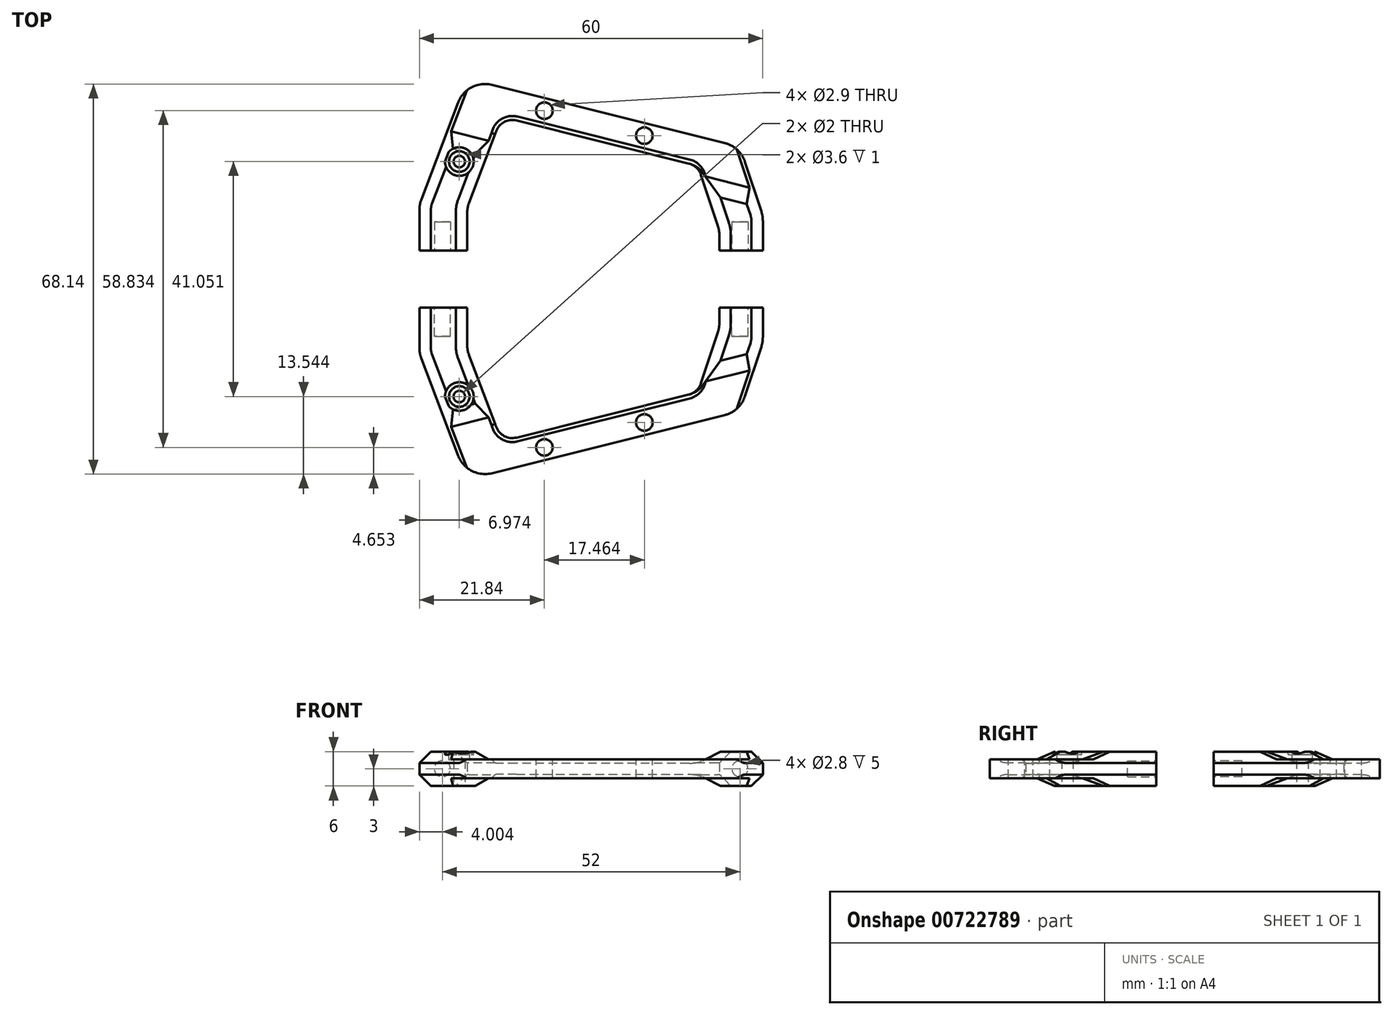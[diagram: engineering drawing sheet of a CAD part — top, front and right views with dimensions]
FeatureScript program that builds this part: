
annotation { "Feature Type Name" : "Feature", "Feature Type Description" : "" }
export const myFeature = defineFeature(function(context is Context, id is Id, definition is map)
    precondition{}
    {
        {
            var Q0;
            Q0=qCreatedBy(makeId("Top.planeOp"),FACE);
            var sketch = newSketch(context, id + "F0", { "sketchPlane" : qUnion([Q0])});
            skLineSegment(sketch, "E0", {"start": v(-36.57, -7.3) * mm, "end": v(-33.72, -7.3) * mm});
            skLineSegment(sketch, "E1", {"start": v(-38.07, -7.3) * mm, "end": v(-38.07, -2.3) * mm, "construction": true});
            skLineSegment(sketch, "E2", {"start": v(13.93, -7.3) * mm, "end": v(13.93, -2.3) * mm, "construction": true});
            skPoint(sketch, "E3", {"position": v(-12.07, -7.3) * mm});
            skLineSegment(sketch, "E4", {"start": v(-12.07, -7.3) * mm, "end": v(3.18, -7.3) * mm});
            skLineSegment(sketch, "E5", {"start": v(-12.07, -7.3) * mm, "end": v(-27.32, -7.3) * mm});
            skLineSegment(sketch, "E6", {"start": v(-42.07, -7.3) * mm, "end": v(-42.07, -0.22) * mm});
            skLineSegment(sketch, "E7", {"start": v(-41.74, 1.56) * mm, "end": v(-35.3, 18.55) * mm});
            skLineSegment(sketch, "E8", {"start": v(17.93, -7.3) * mm, "end": v(17.93, -2.1) * mm});
            skLineSegment(sketch, "E9", {"start": v(17.68, -0.54) * mm, "end": v(14.8, 8.2) * mm});
            skPoint(sketch, "E10", {"position": v(-27.32, -7.3) * mm});
            skPoint(sketch, "E11", {"position": v(3.18, -7.3) * mm});
            skLineSegment(sketch, "E12", {"start": v(-33.72, -7.3) * mm, "end": v(-33.72, -0.77) * mm});
            skLineSegment(sketch, "E13", {"start": v(-29.41, 21.62) * mm, "end": v(11.26, 11.47) * mm});
            skLineSegment(sketch, "E14.3", {"start": v(-25.1, 15.4) * mm, "end": v(5, 7.88) * mm});
            skLineSegment(sketch, "E15.0", {"start": v(-33.4, 1) * mm, "end": v(-28.64, 13.55) * mm});
            skLineSegment(sketch, "E16.0", {"start": v(10.09, -3.05) * mm, "end": v(7.13, 5.91) * mm});
            skPoint(sketch, "E17.visualSharp", {"position": v(-27.7, 16.04) * mm});
            skArc(sketch, "E17.filletArc", {"start": v(-25.1, 15.4) * mm, "mid": v(-27.22, 15.14) * mm, "end": v(-28.64, 13.55) * mm});
            skPoint(sketch, "E18.visualSharp", {"position": v(6.6, 7.48) * mm});
            skArc(sketch, "E18.filletArc", {"start": v(7.13, 5.91) * mm, "mid": v(6.32, 7.17) * mm, "end": v(5, 7.88) * mm});
            skPoint(sketch, "E19.visualSharp", {"position": v(13.93, 10.8) * mm});
            skArc(sketch, "E19.filletArc", {"start": v(14.8, 8.2) * mm, "mid": v(13.45, 10.29) * mm, "end": v(11.26, 11.47) * mm});
            skPoint(sketch, "E20.visualSharp", {"position": v(-33.72, 22.7) * mm});
            skArc(sketch, "E20.filletArc", {"start": v(-29.41, 21.62) * mm, "mid": v(-32.94, 21.2) * mm, "end": v(-35.3, 18.55) * mm});
            skPoint(sketch, "E21.visualSharp", {"position": v(-33.72, 0.14) * mm});
            skArc(sketch, "E21.filletArc", {"start": v(-33.4, 1) * mm, "mid": v(-33.64, 0.13) * mm, "end": v(-33.72, -0.77) * mm});
            skPoint(sketch, "E22.visualSharp", {"position": v(-42.07, 0.7) * mm});
            skArc(sketch, "E22.filletArc", {"start": v(-41.74, 1.56) * mm, "mid": v(-41.98, 0.68) * mm, "end": v(-42.07, -0.22) * mm});
            skPoint(sketch, "E23.visualSharp", {"position": v(17.93, -1.3) * mm});
            skArc(sketch, "E23.filletArc", {"start": v(17.93, -2.1) * mm, "mid": v(17.87, -1.31) * mm, "end": v(17.68, -0.54) * mm});
            skLineSegment(sketch, "E24", {"start": v(10.34, -4.61) * mm, "end": v(10.34, -7.3) * mm});
            skPoint(sketch, "E25.visualSharp", {"position": v(10.34, -3.81) * mm});
            skArc(sketch, "E25.filletArc", {"start": v(10.34, -4.61) * mm, "mid": v(10.27, -3.82) * mm, "end": v(10.09, -3.05) * mm});
            skLineSegment(sketch, "E26.trimOffspring", {"start": v(-33.72, -7.3) * mm, "end": v(-36.57, -7.3) * mm});
            skLineSegment(sketch, "E27.trimOffspring", {"start": v(10.34, -7.3) * mm, "end": v(12.43, -7.3) * mm});
            skLineSegment(sketch, "E28.trimOffspring", {"start": v(-27.32, -7.3) * mm, "end": v(3.18, -7.3) * mm});
            skPoint(sketch, "E29.middle", {"position": v(13.93, -7.3) * mm});
            skPoint(sketch, "E30.middle", {"position": v(-38.07, -7.3) * mm});
            skLineSegment(sketch, "E31.trimOffspring", {"start": v(15.43, -7.3) * mm, "end": v(17.93, -7.3) * mm});
            skLineSegment(sketch, "E32.trimOffspring", {"start": v(-39.57, -7.3) * mm, "end": v(-42.07, -7.3) * mm});
            skLineSegment(sketch, "E33", {"start": v(-39.57, -7.3) * mm, "end": v(-36.57, -7.3) * mm});
            skLineSegment(sketch, "E34", {"start": v(12.43, -7.3) * mm, "end": v(15.43, -7.3) * mm});
            skCircle(sketch, "E35", {"center": v(-35.1, 8.23) * mm, "radius": 1 * mm});
            skSolve(sketch);
        }
        {
            var Q0;
            Q0 = qSketchRegion(id + "F0", true);
            extrude(context, id + "F1", {"entities" : qUnion([Q0]), "depth" : 3.3 * mm, "offsetDistance" : 25 * mm});
        }
        {
            var Q0;
            Q0=makeQuery(id+"F1.opExtrude","CAP_FACE",FACE,{"disambiguationData":[OSD([sQuery(id+"F0.wireOp",EDGE,"E6"),sQuery(id+"F0.wireOp",EDGE,"E7"),sQuery(id+"F0.wireOp",EDGE,"E8"),sQuery(id+"F0.wireOp",EDGE,"E9"),sQuery(id+"F0.wireOp",EDGE,"E12"),sQuery(id+"F0.wireOp",EDGE,"E13"),sQuery(id+"F0.wireOp",EDGE,"m04gNwWP-YN1E-dRtR-cmD1-2egMuyUMC3tO"),sQuery(id+"F0.wireOp",EDGE,"E14.3"),sQuery(id+"F0.wireOp",EDGE,"E15.0"),sQuery(id+"F0.wireOp",EDGE,"E16.0"),sQuery(id+"F0.wireOp",EDGE,"E17.filletArc"),sQuery(id+"F0.wireOp",EDGE,"E18.filletArc"),sQuery(id+"F0.wireOp",EDGE,"E19.filletArc"),sQuery(id+"F0.wireOp",EDGE,"E20.filletArc"),sQuery(id+"F0.wireOp",EDGE,"E21.filletArc"),sQuery(id+"F0.wireOp",EDGE,"E22.filletArc"),sQuery(id+"F0.wireOp",EDGE,"E23.filletArc"),sQuery(id+"F0.wireOp",EDGE,"E24"),sQuery(id+"F0.wireOp",EDGE,"E25.filletArc"),sQuery(id+"F0.wireOp",EDGE,"E26.trimOffspring"),sQuery(id+"F0.wireOp",EDGE,"E27.trimOffspring"),sQuery(id+"F0.wireOp",EDGE,"E31.trimOffspring"),sQuery(id+"F0.wireOp",EDGE,"E32.trimOffspring"),sQuery(id+"F0.wireOp",EDGE,"E33"),sQuery(id+"F0.wireOp",EDGE,"E34")])],"isStart":false});
            cPlane(context, id + "F2", {"entities" : qUnion([Q0]), "cplaneType" : CPlaneType.OFFSET, "offset" : 1.65 * mm, "oppositeDirection" : true, "width" : 150 * mm, "height" : 150 * mm});
        }
        {
            var Q0;
            Q0=qCreatedBy(id+"F2.planeOp",FACE);
            var sketch = newSketch(context, id + "F3", { "sketchPlane" : qUnion([Q0])});
            skLineSegment(sketch, "E36.0", {"start": v(-41.74, 1.56) * mm, "end": v(-37.1, 13.77) * mm});
            skArc(sketch, "E36.1", {"start": v(-41.74, 1.56) * mm, "mid": v(-41.98, 0.68) * mm, "end": v(-42.07, -0.22) * mm});
            skLineSegment(sketch, "E36.2", {"start": v(-42.07, -7.3) * mm, "end": v(-42.07, -0.22) * mm});
            skLineSegment(sketch, "E36.3", {"start": v(-33.4, 1) * mm, "end": v(-29.3, 11.82) * mm});
            skArc(sketch, "E36.4", {"start": v(-33.4, 1) * mm, "mid": v(-33.64, 0.13) * mm, "end": v(-33.72, -0.77) * mm});
            skLineSegment(sketch, "E36.5", {"start": v(-33.72, -7.3) * mm, "end": v(-33.72, -0.77) * mm});
            skLineSegment(sketch, "E36.7", {"start": v(-33.72, -7.3) * mm, "end": v(-42.07, -7.3) * mm});
            skCircle(sketch, "E37.0", {"center": v(-35.1, 8.23) * mm, "radius": 1 * mm});
            skLineSegment(sketch, "E38.0", {"start": v(10.34, -4.61) * mm, "end": v(10.34, -7.3) * mm});
            skLineSegment(sketch, "E38.1", {"start": v(10.09, -3.05) * mm, "end": v(7.13, 5.91) * mm});
            skLineSegment(sketch, "E38.2", {"start": v(17.93, -7.3) * mm, "end": v(17.93, -2.1) * mm});
            skLineSegment(sketch, "E38.3", {"start": v(15.43, -7.3) * mm, "end": v(17.93, -7.3) * mm});
            skLineSegment(sketch, "E38.4", {"start": v(12.43, -7.3) * mm, "end": v(15.43, -7.3) * mm});
            skLineSegment(sketch, "E38.5", {"start": v(10.34, -7.3) * mm, "end": v(12.43, -7.3) * mm});
            skArc(sketch, "E38.6", {"start": v(10.34, -4.61) * mm, "mid": v(10.27, -3.82) * mm, "end": v(10.09, -3.05) * mm});
            skArc(sketch, "E38.7", {"start": v(17.93, -2.1) * mm, "mid": v(17.87, -1.31) * mm, "end": v(17.68, -0.54) * mm});
            skLineSegment(sketch, "E38.8", {"start": v(17.68, -0.54) * mm, "end": v(16.3, 3.62) * mm});
            skLineSegment(sketch, "E39.0", {"start": v(-25.1, 15.4) * mm, "end": v(5, 7.88) * mm});
            skLineSegment(sketch, "E40", {"start": v(-37.1, 13.77) * mm, "end": v(-29.3, 11.82) * mm});
            skLineSegment(sketch, "E41", {"start": v(7.13, 5.91) * mm, "end": v(16.3, 3.62) * mm});
            skPoint(sketch, "E42.orphan", {"position": v(14.8, 8.2) * mm});
            skSolve(sketch);
        }
        {
            var Q0;
            Q0 = qSketchRegion(id + "F3", true);
            extrude(context, id + "F4", {"entities" : qUnion([Q0]), "operationType" : NewBodyOperationType.ADD, "endBound" : BoundingType.SYMMETRIC, "depth" : 6 * mm, "offsetDistance" : 25 * mm});
        }
        {
            var Q0;
            Q0=makeQuery(id+"F1.opExtrude","SWEPT_FACE",FACE,{"disambiguationData":[OSD([sQuery(id+"F0.wireOp",EDGE,"E26.trimOffspring"),sQuery(id+"F0.wireOp",EDGE,"E32.trimOffspring"),sQuery(id+"F0.wireOp",EDGE,"E33")])]});
            var sketch = newSketch(context, id + "F5", { "sketchPlane" : qUnion([Q0])});
            skPoint(sketch, "E43.0", {"position": v(-38.07, 0) * mm});
            skCircle(sketch, "E44", {"center": v(-38.07, 1.65) * mm, "radius": 1.4 * mm});
            skPoint(sketch, "E45.0", {"position": v(-42.07, 1.65) * mm});
            skLineSegment(sketch, "E46", {"start": v(-38.07, 0) * mm, "end": v(-38.07, 4.65) * mm, "construction": true});
            skLineSegment(sketch, "E47", {"start": v(-42.07, 1.65) * mm, "end": v(-33.72, 1.65) * mm, "construction": true});
            skSolve(sketch);
        }
        {
            var Q0;
            {var subQ0=sQuery(id+"F5.wireOp",EDGE,"E44");var subQ1=sQuery(id+"F0.wireOp",EDGE,"E33");var subQ2=sQuery(id+"F0.wireOp",EDGE,"E32.trimOffspring");var subQ3=sQuery(id+"F0.wireOp",EDGE,"E26.trimOffspring");var subQ4=makeQuery(id+"F1.opExtrude","CAP_EDGE",EDGE,{"disambiguationData":[OSD([subQ3,subQ2,subQ1])],"isStart":false});var subQ5=makeQuery(id+"F5.imprint","INTERSECT",VERTEX,{"disambiguationData":[OD(0.0)],"derivedFrom":[subQ4,subQ0]});Q0=makeQuery(id+"F5.imprint","IMPRINT",FACE,{"disambiguationData":[TD([[makeQuery(id+"F5.imprint","IMPRINT",EDGE,{"disambiguationData":[TD([[subQ5,-1.0]])],"derivedFrom":subQ0}),1.0]])]});}
            extrude(context, id + "F6", {"entities" : qUnion([Q0]), "operationType" : NewBodyOperationType.REMOVE, "oppositeDirection" : true, "depth" : 5 * mm, "offsetDistance" : 25 * mm});
        }
        {
            var Q0;
            Q0=makeQuery(id+"F1.opExtrude","SWEPT_FACE",FACE,{"disambiguationData":[OSD([sQuery(id+"F0.wireOp",EDGE,"E27.trimOffspring"),sQuery(id+"F0.wireOp",EDGE,"E31.trimOffspring"),sQuery(id+"F0.wireOp",EDGE,"E34")])]});
            var sketch = newSketch(context, id + "F7", { "sketchPlane" : qUnion([Q0])});
            skPoint(sketch, "E48.0", {"position": v(13.93, 0) * mm});
            skLineSegment(sketch, "E49", {"start": v(13.93, 0) * mm, "end": v(13.93, 3.3) * mm, "construction": true});
            skCircle(sketch, "E50", {"center": v(13.93, 1.65) * mm, "radius": 1.4 * mm});
            skLineSegment(sketch, "E51", {"start": v(10.34, 1.65) * mm, "end": v(17.93, 1.65) * mm, "construction": true});
            skSolve(sketch);
        }
        {
            var Q0;
            Q0 = qSketchRegion(id + "F7", true);
            extrude(context, id + "F8", {"entities" : qUnion([Q0]), "operationType" : NewBodyOperationType.REMOVE, "oppositeDirection" : true, "depth" : 5 * mm, "offsetDistance" : 25 * mm});
        }
        {
            var Q0;
            Q0=makeQuery(id+"F4.opExtrude","CAP_EDGE",EDGE,{"disambiguationData":[OSD([sQuery(id+"F3.wireOp",EDGE,"E36.0")])],"isStart":true});
            var Q1;
            Q1=makeQuery(id+"F4.opExtrude","CAP_EDGE",EDGE,{"disambiguationData":[OSD([sQuery(id+"F3.wireOp",EDGE,"E36.0")])],"isStart":false});
            var Q2;
            Q2=makeQuery(id+"F4.opExtrude","CAP_EDGE",EDGE,{"disambiguationData":[OSD([sQuery(id+"F3.wireOp",EDGE,"E36.2")])],"isStart":false});
            var Q3;
            Q3=makeQuery(id+"F4.opExtrude","CAP_EDGE",EDGE,{"disambiguationData":[OSD([sQuery(id+"F3.wireOp",EDGE,"E36.2")])],"isStart":true});
            var Q4;
            Q4=makeQuery(id+"F4.opExtrude","CAP_EDGE",EDGE,{"disambiguationData":[OSD([sQuery(id+"F3.wireOp",EDGE,"E36.1")])],"isStart":true});
            var Q5;
            Q5=makeQuery(id+"F4.opExtrude","CAP_EDGE",EDGE,{"disambiguationData":[OSD([sQuery(id+"F3.wireOp",EDGE,"E36.1")])],"isStart":false});
            var Q6;
            Q6=makeQuery(id+"F4.opExtrude","CAP_EDGE",EDGE,{"disambiguationData":[OSD([sQuery(id+"F3.wireOp",EDGE,"E36.5")])],"isStart":true});
            var Q7;
            Q7=makeQuery(id+"F4.opExtrude","CAP_EDGE",EDGE,{"disambiguationData":[OSD([sQuery(id+"F3.wireOp",EDGE,"E36.4")])],"isStart":true});
            var Q8;
            Q8=makeQuery(id+"F4.opExtrude","CAP_EDGE",EDGE,{"disambiguationData":[OSD([sQuery(id+"F3.wireOp",EDGE,"E36.3")])],"isStart":true});
            var Q9;
            Q9=makeQuery(id+"F4.opExtrude","CAP_EDGE",EDGE,{"disambiguationData":[OSD([sQuery(id+"F3.wireOp",EDGE,"E36.5")])],"isStart":false});
            var Q10;
            Q10=makeQuery(id+"F4.opExtrude","CAP_EDGE",EDGE,{"disambiguationData":[OSD([sQuery(id+"F3.wireOp",EDGE,"E36.4")])],"isStart":false});
            var Q11;
            Q11=makeQuery(id+"F4.opExtrude","CAP_EDGE",EDGE,{"disambiguationData":[OSD([sQuery(id+"F3.wireOp",EDGE,"E36.3")])],"isStart":false});
            var Q12;
            Q12=makeQuery(id+"F4.opExtrude","CAP_EDGE",EDGE,{"disambiguationData":[OSD([sQuery(id+"F3.wireOp",EDGE,"E38.0")])],"isStart":true});
            var Q13;
            Q13=makeQuery(id+"F4.opExtrude","CAP_EDGE",EDGE,{"disambiguationData":[OSD([sQuery(id+"F3.wireOp",EDGE,"E38.2")])],"isStart":true});
            var Q14;
            Q14=makeQuery(id+"F4.opExtrude","CAP_EDGE",EDGE,{"disambiguationData":[OSD([sQuery(id+"F3.wireOp",EDGE,"E38.2")])],"isStart":false});
            var Q15;
            Q15=makeQuery(id+"F4.opExtrude","CAP_EDGE",EDGE,{"disambiguationData":[OSD([sQuery(id+"F3.wireOp",EDGE,"E38.0")])],"isStart":false});
            chamfer(context, id + "F9", {"entities" : qUnion([Q0, Q1, Q2, Q3, Q4, Q5, Q6, Q7, Q8, Q9, Q10, Q11, Q12, Q13, Q14, Q15]), "width" : 2 * mm, "tangentPropagation" : true});
        }
        {
            var Q0;
            Q0=makeQuery(id+"F4.opExtrude","CAP_EDGE",EDGE,{"disambiguationData":[OSD([sQuery(id+"F3.wireOp",EDGE,"E41")])],"isStart":true});
            var Q1;
            Q1=makeQuery(id+"F4.opExtrude","CAP_EDGE",EDGE,{"disambiguationData":[OSD([sQuery(id+"F3.wireOp",EDGE,"E40")])],"isStart":true});
            chamfer(context, id + "F10", {"entities" : qUnion([Q0, Q1]), "chamferType" : ChamferType.TWO_OFFSETS, "width1" : 3 * mm, "oppositeDirection" : false, "width2" : 1.4 * mm, "tangentPropagation" : true});
        }
        {
            var Q0;
            Q0=makeQuery(id+"F4.opExtrude","CAP_EDGE",EDGE,{"disambiguationData":[OSD([sQuery(id+"F3.wireOp",EDGE,"E40")])],"isStart":false});
            var Q1;
            Q1=makeQuery(id+"F4.opExtrude","CAP_EDGE",EDGE,{"disambiguationData":[OSD([sQuery(id+"F3.wireOp",EDGE,"E41")])],"isStart":false});
            chamfer(context, id + "F11", {"entities" : qUnion([Q0, Q1]), "chamferType" : ChamferType.TWO_OFFSETS, "width1" : 1.4 * mm, "oppositeDirection" : false, "width2" : 3 * mm, "tangentPropagation" : true});
        }
        {
            var Q0;
            Q0=makeQuery(id+"F1.opExtrude","CAP_EDGE",EDGE,{"disambiguationData":[OSD([sQuery(id+"F0.wireOp",EDGE,"E14.3")])],"isStart":false});
            var Q1;
            Q1=makeQuery(id+"F1.opExtrude","CAP_EDGE",EDGE,{"disambiguationData":[OSD([sQuery(id+"F0.wireOp",EDGE,"E14.3")])],"isStart":true});
            chamfer(context, id + "F12", {"entities" : qUnion([Q0, Q1]), "width" : .7 * mm, "tangentPropagation" : true});
        }
        {
            var Q0;
            Q0=makeQuery(id+"F4.opExtrude","CAP_FACE",FACE,{"disambiguationData":[OSD([sQuery(id+"F3.wireOp",EDGE,"E36.0"),sQuery(id+"F3.wireOp",EDGE,"E36.1"),sQuery(id+"F3.wireOp",EDGE,"E36.2"),sQuery(id+"F3.wireOp",EDGE,"E36.3"),sQuery(id+"F3.wireOp",EDGE,"E36.4"),sQuery(id+"F3.wireOp",EDGE,"E36.5"),sQuery(id+"F3.wireOp",EDGE,"E36.7"),sQuery(id+"F3.wireOp",EDGE,"E37.0"),sQuery(id+"F3.wireOp",EDGE,"E40")])],"isStart":false});
            var sketch = newSketch(context, id + "F13", { "sketchPlane" : qUnion([Q0])});
            skCircle(sketch, "E52", {"center": v(-35.1, 8.23) * mm, "radius": 2.5 * mm});
            skCircle(sketch, "E53", {"center": v(-35.1, 8.23) * mm, "radius": 1.8 * mm});
            skSolve(sketch);
        }
        {
            var Q0;
            Q0=makeQuery(id+"F1.opExtrude","CAP_FACE",FACE,{"disambiguationData":[OSD([sQuery(id+"F0.wireOp",EDGE,"E6"),sQuery(id+"F0.wireOp",EDGE,"E7"),sQuery(id+"F0.wireOp",EDGE,"E8"),sQuery(id+"F0.wireOp",EDGE,"E9"),sQuery(id+"F0.wireOp",EDGE,"E12"),sQuery(id+"F0.wireOp",EDGE,"E13"),sQuery(id+"F0.wireOp",EDGE,"E14.3"),sQuery(id+"F0.wireOp",EDGE,"E15.0"),sQuery(id+"F0.wireOp",EDGE,"E16.0"),sQuery(id+"F0.wireOp",EDGE,"E17.filletArc"),sQuery(id+"F0.wireOp",EDGE,"E18.filletArc"),sQuery(id+"F0.wireOp",EDGE,"E19.filletArc"),sQuery(id+"F0.wireOp",EDGE,"E20.filletArc"),sQuery(id+"F0.wireOp",EDGE,"E21.filletArc"),sQuery(id+"F0.wireOp",EDGE,"E22.filletArc"),sQuery(id+"F0.wireOp",EDGE,"E23.filletArc"),sQuery(id+"F0.wireOp",EDGE,"E24"),sQuery(id+"F0.wireOp",EDGE,"E25.filletArc"),sQuery(id+"F0.wireOp",EDGE,"E26.trimOffspring"),sQuery(id+"F0.wireOp",EDGE,"E27.trimOffspring"),sQuery(id+"F0.wireOp",EDGE,"E31.trimOffspring"),sQuery(id+"F0.wireOp",EDGE,"E32.trimOffspring"),sQuery(id+"F0.wireOp",EDGE,"E33"),sQuery(id+"F0.wireOp",EDGE,"E34"),sQuery(id+"F0.wireOp",EDGE,"E35")])],"isStart":false});
            var sketch = newSketch(context, id + "F14", { "sketchPlane" : qUnion([Q0])});
            skLineSegment(sketch, "E54", {"start": v(-20.23, 17.12) * mm, "end": v(-2.77, 12.76) * mm});
            skCircle(sketch, "E55", {"center": v(-20.23, 17.12) * mm, "radius": 1.45 * mm});
            skCircle(sketch, "E56", {"center": v(-2.77, 12.76) * mm, "radius": 1.45 * mm});
            skLineSegment(sketch, "E57", {"start": v(-15.94, 18.26) * mm, "end": v(-16.99, 14.1) * mm});
            skPoint(sketch, "E58", {"position": v(-16.46, 16.18) * mm});
            skLineSegment(sketch, "E59", {"start": v(-29.41, 21.62) * mm, "end": v(-30.5, 17.24) * mm});
            skSolve(sketch);
        }
        {
            var Q0;
            Q0=makeQuery(id+"F14.imprint","IMPRINT",FACE,{"disambiguationData":[TD([[makeQuery(id+"F14.imprint","IMPRINT",EDGE,{"derivedFrom":sQuery(id+"F14.wireOp",EDGE,"E55")}),1.0]])]});
            var Q1;
            Q1=makeQuery(id+"F14.imprint","IMPRINT",FACE,{"disambiguationData":[TD([[makeQuery(id+"F14.imprint","IMPRINT",EDGE,{"derivedFrom":sQuery(id+"F14.wireOp",EDGE,"E56")}),1.0]])]});
            extrude(context, id + "F15", {"entities" : qUnion([Q0, Q1]), "operationType" : NewBodyOperationType.REMOVE, "oppositeDirection" : true, "depth" : 25 * mm, "offsetDistance" : 25 * mm});
        }
        {
            var Q0;
            Q0=makeQuery(id+"F13.imprint","IMPRINT",FACE,{"disambiguationData":[TD([[makeQuery(id+"F13.imprint","IMPRINT",EDGE,{"derivedFrom":sQuery(id+"F13.wireOp",EDGE,"E53")}),-1.0]])]});
            var Q1;
            {var subQ0=sQuery(id+"F13.wireOp",EDGE,"E52");var subQ1=sQuery(id+"F3.wireOp",EDGE,"E36.0");var subQ2=makeQuery(id+"F9.opChamfer","BLEND_EDGE",EDGE,{"blendedFrom":[makeQuery(id+"F4.opExtrude","CAP_EDGE",EDGE,{"disambiguationData":[OSD([subQ1])],"isStart":false}),makeQuery(id+"F4.opExtrude","CAP_FACE",FACE,{"disambiguationData":[OSD([subQ1,sQuery(id+"F3.wireOp",EDGE,"E36.1"),sQuery(id+"F3.wireOp",EDGE,"E36.2"),sQuery(id+"F3.wireOp",EDGE,"E36.3"),sQuery(id+"F3.wireOp",EDGE,"E36.4"),sQuery(id+"F3.wireOp",EDGE,"E36.5"),sQuery(id+"F3.wireOp",EDGE,"E36.7"),sQuery(id+"F3.wireOp",EDGE,"E37.0"),sQuery(id+"F3.wireOp",EDGE,"E40")])],"isStart":false})],"blendedInto":[makeQuery(id+"F4.opExtrude","CAP_FACE",FACE,{"disambiguationData":[OSD([subQ1,sQuery(id+"F3.wireOp",EDGE,"E36.1"),sQuery(id+"F3.wireOp",EDGE,"E36.2"),sQuery(id+"F3.wireOp",EDGE,"E36.3"),sQuery(id+"F3.wireOp",EDGE,"E36.4"),sQuery(id+"F3.wireOp",EDGE,"E36.5"),sQuery(id+"F3.wireOp",EDGE,"E36.7"),sQuery(id+"F3.wireOp",EDGE,"E37.0"),sQuery(id+"F3.wireOp",EDGE,"E40")])],"isStart":false})]});var subQ3=makeQuery(id+"F13.imprint","INTERSECT",VERTEX,{"disambiguationData":[OD(0.0)],"derivedFrom":[subQ2,subQ0]});Q1=makeQuery(id+"F13.imprint","IMPRINT",FACE,{"disambiguationData":[TD([[makeQuery(id+"F13.imprint","IMPRINT",EDGE,{"disambiguationData":[TD([[subQ3,-1.0]])],"derivedFrom":subQ0}),1.0]])]});}
            var Q2;
            {var subQ0=sQuery(id+"F13.wireOp",EDGE,"E52");var subQ1=sQuery(id+"F3.wireOp",EDGE,"E40");var subQ2=makeQuery(id+"F11.opChamfer","BLEND_EDGE",EDGE,{"blendedFrom":[makeQuery(id+"F4.opExtrude","CAP_EDGE",EDGE,{"disambiguationData":[OSD([subQ1])],"isStart":false}),makeQuery(id+"F4.opExtrude","CAP_FACE",FACE,{"disambiguationData":[OSD([sQuery(id+"F3.wireOp",EDGE,"E36.0"),sQuery(id+"F3.wireOp",EDGE,"E36.1"),sQuery(id+"F3.wireOp",EDGE,"E36.2"),sQuery(id+"F3.wireOp",EDGE,"E36.3"),sQuery(id+"F3.wireOp",EDGE,"E36.4"),sQuery(id+"F3.wireOp",EDGE,"E36.5"),sQuery(id+"F3.wireOp",EDGE,"E36.7"),sQuery(id+"F3.wireOp",EDGE,"E37.0"),subQ1])],"isStart":false})],"blendedInto":[makeQuery(id+"F4.opExtrude","CAP_FACE",FACE,{"disambiguationData":[OSD([sQuery(id+"F3.wireOp",EDGE,"E36.0"),sQuery(id+"F3.wireOp",EDGE,"E36.1"),sQuery(id+"F3.wireOp",EDGE,"E36.2"),sQuery(id+"F3.wireOp",EDGE,"E36.3"),sQuery(id+"F3.wireOp",EDGE,"E36.4"),sQuery(id+"F3.wireOp",EDGE,"E36.5"),sQuery(id+"F3.wireOp",EDGE,"E36.7"),sQuery(id+"F3.wireOp",EDGE,"E37.0"),subQ1])],"isStart":false})]});var subQ3=makeQuery(id+"F13.imprint","INTERSECT",VERTEX,{"disambiguationData":[OD(0.0)],"derivedFrom":[subQ2,subQ0]});Q2=makeQuery(id+"F13.imprint","IMPRINT",FACE,{"disambiguationData":[TD([[makeQuery(id+"F13.imprint","IMPRINT",EDGE,{"disambiguationData":[TD([[subQ3,-1.0]])],"derivedFrom":subQ0}),1.0]])]});}
            var Q3;
            {var subQ0=sQuery(id+"F13.wireOp",EDGE,"E52");var subQ1=sQuery(id+"F3.wireOp",EDGE,"E36.3");var subQ2=makeQuery(id+"F9.opChamfer","BLEND_EDGE",EDGE,{"blendedFrom":[makeQuery(id+"F4.opExtrude","CAP_EDGE",EDGE,{"disambiguationData":[OSD([subQ1])],"isStart":false}),makeQuery(id+"F4.opExtrude","CAP_FACE",FACE,{"disambiguationData":[OSD([sQuery(id+"F3.wireOp",EDGE,"E36.0"),sQuery(id+"F3.wireOp",EDGE,"E36.1"),sQuery(id+"F3.wireOp",EDGE,"E36.2"),subQ1,sQuery(id+"F3.wireOp",EDGE,"E36.4"),sQuery(id+"F3.wireOp",EDGE,"E36.5"),sQuery(id+"F3.wireOp",EDGE,"E36.7"),sQuery(id+"F3.wireOp",EDGE,"E37.0"),sQuery(id+"F3.wireOp",EDGE,"E40")])],"isStart":false})],"blendedInto":[makeQuery(id+"F4.opExtrude","CAP_FACE",FACE,{"disambiguationData":[OSD([sQuery(id+"F3.wireOp",EDGE,"E36.0"),sQuery(id+"F3.wireOp",EDGE,"E36.1"),sQuery(id+"F3.wireOp",EDGE,"E36.2"),subQ1,sQuery(id+"F3.wireOp",EDGE,"E36.4"),sQuery(id+"F3.wireOp",EDGE,"E36.5"),sQuery(id+"F3.wireOp",EDGE,"E36.7"),sQuery(id+"F3.wireOp",EDGE,"E37.0"),sQuery(id+"F3.wireOp",EDGE,"E40")])],"isStart":false})]});var subQ3=makeQuery(id+"F13.imprint","INTERSECT",VERTEX,{"disambiguationData":[OD(0.0)],"derivedFrom":[subQ2,subQ0]});Q3=makeQuery(id+"F13.imprint","IMPRINT",FACE,{"disambiguationData":[TD([[makeQuery(id+"F13.imprint","IMPRINT",EDGE,{"disambiguationData":[TD([[subQ3,1.0]])],"derivedFrom":subQ0}),1.0]])]});}
            extrude(context, id + "F16", {"entities" : qUnion([Q0, Q1, Q2, Q3]), "operationType" : NewBodyOperationType.REMOVE, "oppositeDirection" : true, "depth" : .5 * mm, "offsetDistance" : 25 * mm});
        }
        {
            var Q0;
            {var subQ0=sQuery(id+"F3.wireOp",EDGE,"E37.0");Q0=makeQuery(id+"F16.boolean.opBoolean","SPLIT",FACE,{"disambiguationData":[TD([makeQuery(id+"F1.opExtrude","SWEPT_FACE",FACE,{"disambiguationData":[OSD([sQuery(id+"F0.wireOp",EDGE,"E35")])]}),makeQuery(id+"F4.opExtrude","SWEPT_FACE",FACE,{"disambiguationData":[OSD([subQ0])]}),makeQuery(id+"F16.opExtrude","SWEPT_FACE",FACE,{"disambiguationData":[OSD([sQuery(id+"F13.wireOp",EDGE,"E53")])]})])],"derivedFrom":makeQuery(id+"F4.opExtrude","CAP_FACE",FACE,{"disambiguationData":[OSD([sQuery(id+"F3.wireOp",EDGE,"E36.0"),sQuery(id+"F3.wireOp",EDGE,"E36.1"),sQuery(id+"F3.wireOp",EDGE,"E36.2"),sQuery(id+"F3.wireOp",EDGE,"E36.3"),sQuery(id+"F3.wireOp",EDGE,"E36.4"),sQuery(id+"F3.wireOp",EDGE,"E36.5"),sQuery(id+"F3.wireOp",EDGE,"E36.7"),subQ0,sQuery(id+"F3.wireOp",EDGE,"E40")])],"isStart":false})});}
            extrude(context, id + "F17", {"entities" : qUnion([Q0]), "operationType" : NewBodyOperationType.REMOVE, "oppositeDirection" : true, "depth" : 1.5 * mm, "offsetDistance" : 25 * mm});
        }
        {
            var Q0;
            Q0=makeQuery(id+"F4.boolean.opBoolean","MERGE",FACE,{"derivedFrom":[makeQuery(id+"F1.opExtrude","SWEPT_FACE",FACE,{"disambiguationData":[OSD([sQuery(id+"F0.wireOp",EDGE,"E0"),sQuery(id+"F0.wireOp",EDGE,"E32.trimOffspring"),sQuery(id+"F0.wireOp",EDGE,"E33")])]}),makeQuery(id+"F4.opExtrude","SWEPT_FACE",FACE,{"disambiguationData":[OSD([sQuery(id+"F3.wireOp",EDGE,"E36.7")])]})]});
            var Q1;
            Q1=makeQuery(id+"F4.boolean.opBoolean","MERGE",FACE,{"derivedFrom":[makeQuery(id+"F1.opExtrude","SWEPT_FACE",FACE,{"disambiguationData":[OSD([sQuery(id+"F0.wireOp",EDGE,"E27.trimOffspring"),sQuery(id+"F0.wireOp",EDGE,"E31.trimOffspring"),sQuery(id+"F0.wireOp",EDGE,"E34")])]}),makeQuery(id+"F4.opExtrude","SWEPT_FACE",FACE,{"disambiguationData":[OSD([sQuery(id+"F3.wireOp",EDGE,"E38.3"),sQuery(id+"F3.wireOp",EDGE,"E38.4"),sQuery(id+"F3.wireOp",EDGE,"E38.5")])]})]});
            cPlane(context, id + "F18", {"entities" : qUnion([Q0, Q1]), "cplaneType" : CPlaneType.MID_PLANE, "offset" : 25 * mm, "width" : 150 * mm, "height" : 150 * mm});
        }
        {
            var Q0;
            Q0=qCreatedBy(id+"F18.planeOp",FACE);
            cPlane(context, id + "F19", {"entities" : qUnion([Q0]), "cplaneType" : CPlaneType.OFFSET, "offset" : 5 * mm, "width" : 150 * mm, "height" : 150 * mm});
        }
        {
            var Q0;
            Q0=makeQuery(id+"F1.opExtrude","SWEPT_BODY",BODY,{"disambiguationData":[OSD([sQuery(id+"F0.wireOp",EDGE,"E0"),sQuery(id+"F0.wireOp",EDGE,"E6"),sQuery(id+"F0.wireOp",EDGE,"E7"),sQuery(id+"F0.wireOp",EDGE,"E8"),sQuery(id+"F0.wireOp",EDGE,"E9"),sQuery(id+"F0.wireOp",EDGE,"E12"),sQuery(id+"F0.wireOp",EDGE,"E13"),sQuery(id+"F0.wireOp",EDGE,"E14.3"),sQuery(id+"F0.wireOp",EDGE,"E15.0"),sQuery(id+"F0.wireOp",EDGE,"E16.0"),sQuery(id+"F0.wireOp",EDGE,"E17.filletArc"),sQuery(id+"F0.wireOp",EDGE,"E18.filletArc"),sQuery(id+"F0.wireOp",EDGE,"E19.filletArc"),sQuery(id+"F0.wireOp",EDGE,"E20.filletArc"),sQuery(id+"F0.wireOp",EDGE,"E21.filletArc"),sQuery(id+"F0.wireOp",EDGE,"E22.filletArc"),sQuery(id+"F0.wireOp",EDGE,"E23.filletArc"),sQuery(id+"F0.wireOp",EDGE,"E24"),sQuery(id+"F0.wireOp",EDGE,"E25.filletArc"),sQuery(id+"F0.wireOp",EDGE,"E27.trimOffspring"),sQuery(id+"F0.wireOp",EDGE,"E31.trimOffspring"),sQuery(id+"F0.wireOp",EDGE,"E32.trimOffspring"),sQuery(id+"F0.wireOp",EDGE,"E33"),sQuery(id+"F0.wireOp",EDGE,"E34"),sQuery(id+"F0.wireOp",EDGE,"E35")])]});
            var Q1;
            Q1=qCreatedBy(id+"F19.planeOp",FACE);
            mirror(context, id + "F20", {"entities" : qUnion([Q0]), "mirrorPlane" : qUnion([Q1])});
        }
    });
